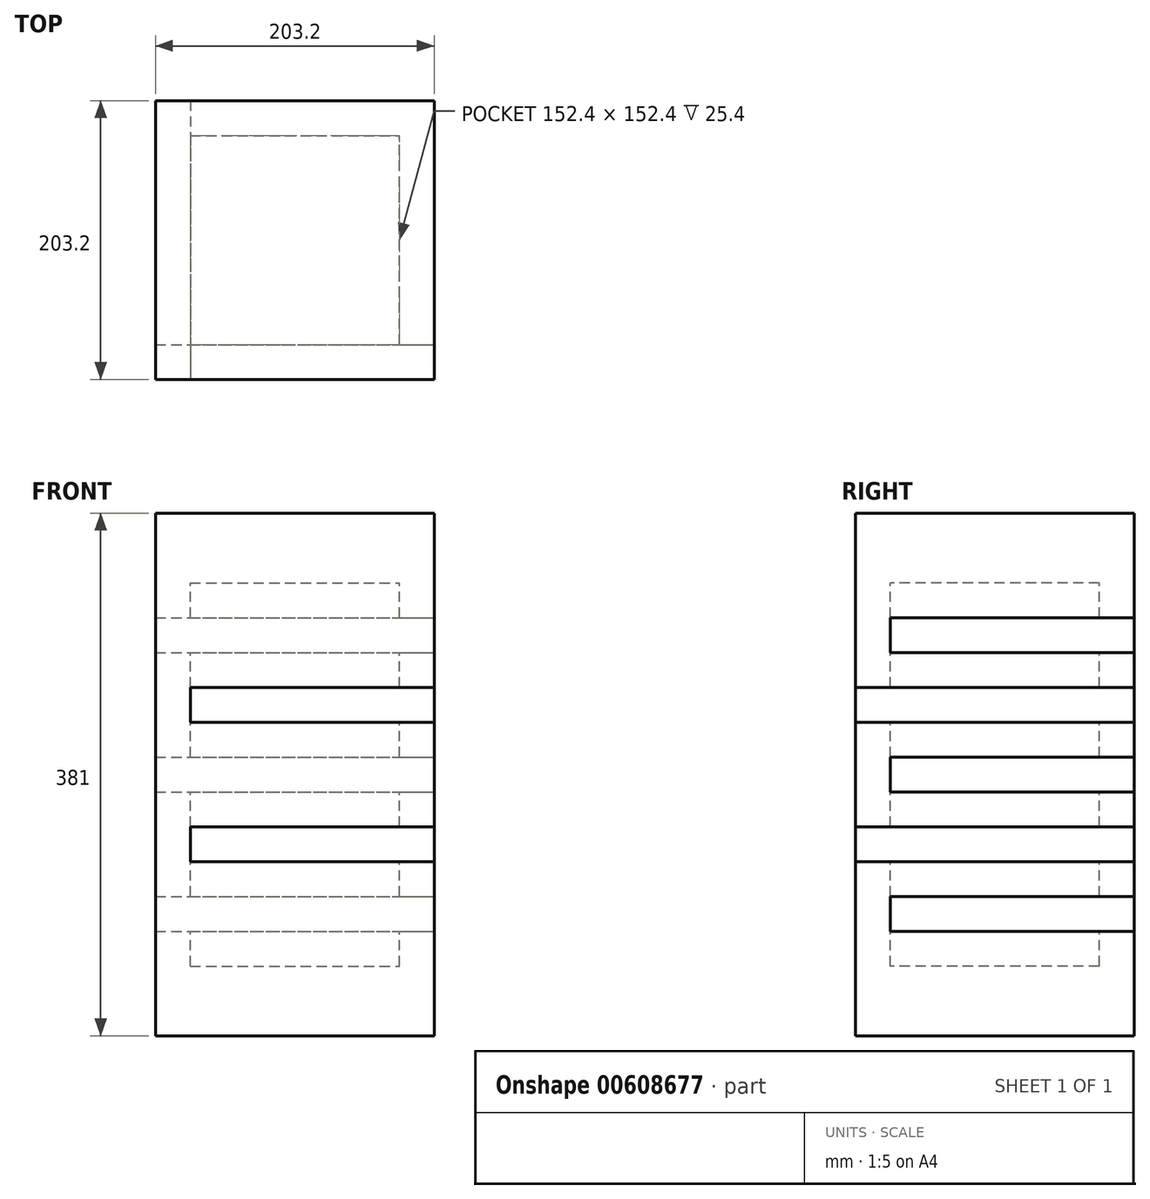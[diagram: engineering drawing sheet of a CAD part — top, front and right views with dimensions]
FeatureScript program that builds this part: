
annotation { "Feature Type Name" : "Feature", "Feature Type Description" : "" }
export const myFeature = defineFeature(function(context is Context, id is Id, definition is map)
    precondition{}
    {
        {
            var Q0;
            Q0=qCreatedBy(makeId("Front.planeOp"),FACE);
            var sketch = newSketch(context, id + "F0", { "sketchPlane" : qUnion([Q0])});
            skLineSegment(sketch, "E0.bottom", {"start": v(0, 0) * mm, "end": v(203.2, 0) * mm});
            skLineSegment(sketch, "E0.top", {"start": v(0, 381) * mm, "end": v(203.2, 381) * mm});
            skLineSegment(sketch, "E0.left", {"start": v(0, 0) * mm, "end": v(0, 381) * mm});
            skLineSegment(sketch, "E0.right", {"start": v(203.2, 0) * mm, "end": v(203.2, 381) * mm});
            skSolve(sketch);
        }
        {
            var Q0;
            Q0=makeQuery(id+"F0.imprint","IMPRINT",FACE,{"disambiguationData":[TD([[makeQuery(id+"F0.imprint","IMPRINT",EDGE,{"derivedFrom":sQuery(id+"F0.wireOp",EDGE,"E0.bottom")}),1.0]])]});
            extrude(context, id + "F1", {"entities" : qUnion([Q0]), "depth" : 203.2 * mm, "offsetDistance" : 25.4 * mm});
        }
        {
            var Q0;
            Q0=makeQuery(id+"F1.opExtrude","CAP_FACE",FACE,{"disambiguationData":[OSD([sQuery(id+"F0.wireOp",EDGE,"E0.bottom"),sQuery(id+"F0.wireOp",EDGE,"E0.top"),sQuery(id+"F0.wireOp",EDGE,"E0.left"),sQuery(id+"F0.wireOp",EDGE,"E0.right")])],"isStart":false});
            var sketch = newSketch(context, id + "F2", { "sketchPlane" : qUnion([Q0])});
            skLineSegment(sketch, "E1.bottom", {"start": v(203.2, 355.6) * mm, "end": v(25.4, 355.6) * mm});
            skLineSegment(sketch, "E1.top", {"start": v(203.2, 330.2) * mm, "end": v(25.4, 330.2) * mm});
            skLineSegment(sketch, "E1.left", {"start": v(203.2, 355.6) * mm, "end": v(203.2, 330.2) * mm});
            skLineSegment(sketch, "E1.right", {"start": v(25.4, 355.6) * mm, "end": v(25.4, 330.2) * mm});
            skLineSegment(sketch, "E2.bottom", {"start": v(203.2, 254) * mm, "end": v(25.4, 254) * mm});
            skLineSegment(sketch, "E2.top", {"start": v(203.2, 228.6) * mm, "end": v(25.4, 228.6) * mm});
            skLineSegment(sketch, "E2.left", {"start": v(203.2, 254) * mm, "end": v(203.2, 228.6) * mm});
            skLineSegment(sketch, "E2.right", {"start": v(25.4, 254) * mm, "end": v(25.4, 228.6) * mm});
            skLineSegment(sketch, "E3.bottom", {"start": v(203.2, 152.4) * mm, "end": v(25.4, 152.4) * mm});
            skLineSegment(sketch, "E3.top", {"start": v(203.2, 127) * mm, "end": v(25.4, 127) * mm});
            skLineSegment(sketch, "E3.left", {"start": v(203.2, 152.4) * mm, "end": v(203.2, 127) * mm});
            skLineSegment(sketch, "E3.right", {"start": v(25.4, 152.4) * mm, "end": v(25.4, 127) * mm});
            skLineSegment(sketch, "E4.bottom", {"start": v(203.2, 50.8) * mm, "end": v(25.4, 50.8) * mm});
            skLineSegment(sketch, "E4.top", {"start": v(203.2, 25.4) * mm, "end": v(25.4, 25.4) * mm});
            skLineSegment(sketch, "E4.left", {"start": v(203.2, 50.8) * mm, "end": v(203.2, 25.4) * mm});
            skLineSegment(sketch, "E4.right", {"start": v(25.4, 50.8) * mm, "end": v(25.4, 25.4) * mm});
            skSolve(sketch);
        }
        {
            var Q0;
            Q0=makeQuery(id+"F2.imprint","IMPRINT",FACE,{"disambiguationData":[TD([[makeQuery(id+"F2.imprint","IMPRINT",EDGE,{"derivedFrom":sQuery(id+"F2.wireOp",EDGE,"E1.bottom")}),1.0]])]});
            var Q1;
            Q1=makeQuery(id+"F2.imprint","IMPRINT",FACE,{"disambiguationData":[TD([[makeQuery(id+"F2.imprint","IMPRINT",EDGE,{"derivedFrom":sQuery(id+"F2.wireOp",EDGE,"E2.bottom")}),1.0]])]});
            var Q2;
            Q2=makeQuery(id+"F2.imprint","IMPRINT",FACE,{"disambiguationData":[TD([[makeQuery(id+"F2.imprint","IMPRINT",EDGE,{"derivedFrom":sQuery(id+"F2.wireOp",EDGE,"E3.bottom")}),1.0]])]});
            var Q3;
            Q3=makeQuery(id+"F2.imprint","IMPRINT",FACE,{"disambiguationData":[TD([[makeQuery(id+"F2.imprint","IMPRINT",EDGE,{"derivedFrom":sQuery(id+"F2.wireOp",EDGE,"E4.bottom")}),1.0]])]});
            extrude(context, id + "F3", {"entities" : qUnion([Q0, Q1, Q2, Q3]), "operationType" : NewBodyOperationType.REMOVE, "endBound" : BoundingType.THROUGH_ALL, "oppositeDirection" : true, "depth" : 25.4 * mm, "offsetDistance" : 25.4 * mm});
        }
        {
            var Q0;
            {var subQ0=sQuery(id+"F0.wireOp",EDGE,"E0.right");Q0=makeQuery(id+"F3.boolean.opBoolean","SPLIT",FACE,{"disambiguationData":[TD([makeQuery(id+"F3.opExtrude","SWEPT_FACE",FACE,{"disambiguationData":[OSD([sQuery(id+"F2.wireOp",EDGE,"E1.top")])]})])],"derivedFrom":makeQuery(id+"F1.opExtrude","SWEPT_FACE",FACE,{"disambiguationData":[OSD([subQ0])]})});}
            var sketch = newSketch(context, id + "F4", { "sketchPlane" : qUnion([Q0])});
            skLineSegment(sketch, "E5.bottom", {"start": v(0, 304.8) * mm, "end": v(-177.8, 304.8) * mm});
            skLineSegment(sketch, "E5.top", {"start": v(0, 279.4) * mm, "end": v(-177.8, 279.4) * mm});
            skLineSegment(sketch, "E5.left", {"start": v(0, 304.8) * mm, "end": v(0, 279.4) * mm});
            skLineSegment(sketch, "E5.right", {"start": v(-177.8, 304.8) * mm, "end": v(-177.8, 279.4) * mm});
            skLineSegment(sketch, "E6.bottom", {"start": v(0, 203.2) * mm, "end": v(-177.8, 203.2) * mm});
            skLineSegment(sketch, "E6.top", {"start": v(0, 177.8) * mm, "end": v(-177.8, 177.8) * mm});
            skLineSegment(sketch, "E6.left", {"start": v(0, 203.2) * mm, "end": v(0, 177.8) * mm});
            skLineSegment(sketch, "E6.right", {"start": v(-177.8, 203.2) * mm, "end": v(-177.8, 177.8) * mm});
            skLineSegment(sketch, "E7.bottom", {"start": v(0, 101.6) * mm, "end": v(-177.8, 101.6) * mm});
            skLineSegment(sketch, "E7.top", {"start": v(0, 76.2) * mm, "end": v(-177.8, 76.2) * mm});
            skLineSegment(sketch, "E7.left", {"start": v(0, 101.6) * mm, "end": v(0, 76.2) * mm});
            skLineSegment(sketch, "E7.right", {"start": v(-177.8, 101.6) * mm, "end": v(-177.8, 76.2) * mm});
            skSolve(sketch);
        }
        {
            var Q0;
            Q0=makeQuery(id+"F4.imprint","IMPRINT",FACE,{"disambiguationData":[TD([[makeQuery(id+"F4.imprint","IMPRINT",EDGE,{"derivedFrom":sQuery(id+"F4.wireOp",EDGE,"E5.bottom")}),1.0]])]});
            var Q1;
            Q1=makeQuery(id+"F4.imprint","IMPRINT",FACE,{"disambiguationData":[TD([[makeQuery(id+"F4.imprint","IMPRINT",EDGE,{"derivedFrom":sQuery(id+"F4.wireOp",EDGE,"E6.bottom")}),1.0]])]});
            var Q2;
            Q2=makeQuery(id+"F4.imprint","IMPRINT",FACE,{"disambiguationData":[TD([[makeQuery(id+"F4.imprint","IMPRINT",EDGE,{"derivedFrom":sQuery(id+"F4.wireOp",EDGE,"E7.bottom")}),1.0]])]});
            extrude(context, id + "F5", {"entities" : qUnion([Q0, Q1, Q2]), "operationType" : NewBodyOperationType.REMOVE, "endBound" : BoundingType.THROUGH_ALL, "oppositeDirection" : true, "depth" : 25.4 * mm, "offsetDistance" : 25.4 * mm});
        }
        {
            var Q0;
            Q0=makeQuery(id+"F1.opExtrude","SWEPT_FACE",FACE,{"disambiguationData":[OSD([sQuery(id+"F0.wireOp",EDGE,"E0.top")])]});
            var sketch = newSketch(context, id + "F6", { "sketchPlane" : qUnion([Q0])});
            skLineSegment(sketch, "E8.0", {"start": v(25.4, -177.8) * mm, "end": v(25.4, -25.4) * mm});
            skLineSegment(sketch, "E8.1", {"start": v(25.4, -177.8) * mm, "end": v(177.8, -177.8) * mm});
            skLineSegment(sketch, "E8.2", {"start": v(177.8, -177.8) * mm, "end": v(177.8, -25.4) * mm});
            skLineSegment(sketch, "E8.3", {"start": v(25.4, -25.4) * mm, "end": v(177.8, -25.4) * mm});
            skSolve(sketch);
        }
        {
            var Q0;
            Q0=makeQuery(id+"F6.imprint","IMPRINT",FACE,{"disambiguationData":[TD([[makeQuery(id+"F6.imprint","IMPRINT",EDGE,{"derivedFrom":sQuery(id+"F6.wireOp",EDGE,"E8.0")}),-1.0]])]});
            extrude(context, id + "F7", {"entities" : qUnion([Q0]), "operationType" : NewBodyOperationType.REMOVE, "endBound" : BoundingType.THROUGH_ALL, "oppositeDirection" : true, "depth" : 25.4 * mm, "offsetDistance" : 25.4 * mm});
        }
        {
            var Q0;
            Q0=makeQuery(id+"F2.imprint","IMPRINT",FACE,{"disambiguationData":[TD([[makeQuery(id+"F2.imprint","IMPRINT",EDGE,{"derivedFrom":sQuery(id+"F2.wireOp",EDGE,"E1.bottom")}),1.0]])]});
            var Q1;
            Q1=makeQuery(id+"F2.imprint","IMPRINT",FACE,{"disambiguationData":[TD([[makeQuery(id+"F2.imprint","IMPRINT",EDGE,{"derivedFrom":sQuery(id+"F2.wireOp",EDGE,"E2.bottom")}),1.0]])]});
            var Q2;
            Q2=makeQuery(id+"F2.imprint","IMPRINT",FACE,{"disambiguationData":[TD([[makeQuery(id+"F2.imprint","IMPRINT",EDGE,{"derivedFrom":sQuery(id+"F2.wireOp",EDGE,"E3.bottom")}),1.0]])]});
            var Q3;
            Q3=makeQuery(id+"F2.imprint","IMPRINT",FACE,{"disambiguationData":[TD([[makeQuery(id+"F2.imprint","IMPRINT",EDGE,{"derivedFrom":sQuery(id+"F2.wireOp",EDGE,"E4.bottom")}),1.0]])]});
            extrude(context, id + "F8", {"entities" : qUnion([Q0, Q1, Q2, Q3]), "oppositeDirection" : true, "depth" : 203.2 * mm, "offsetDistance" : 25.4 * mm});
        }
        {
            var Q0;
            Q0=makeQuery(id+"F4.imprint","IMPRINT",FACE,{"disambiguationData":[TD([[makeQuery(id+"F4.imprint","IMPRINT",EDGE,{"derivedFrom":sQuery(id+"F4.wireOp",EDGE,"E5.bottom")}),1.0]])]});
            var Q1;
            Q1=makeQuery(id+"F4.imprint","IMPRINT",FACE,{"disambiguationData":[TD([[makeQuery(id+"F4.imprint","IMPRINT",EDGE,{"derivedFrom":sQuery(id+"F4.wireOp",EDGE,"E6.bottom")}),1.0]])]});
            var Q2;
            Q2=makeQuery(id+"F4.imprint","IMPRINT",FACE,{"disambiguationData":[TD([[makeQuery(id+"F4.imprint","IMPRINT",EDGE,{"derivedFrom":sQuery(id+"F4.wireOp",EDGE,"E7.bottom")}),1.0]])]});
            extrude(context, id + "F9", {"entities" : qUnion([Q0, Q1, Q2]), "oppositeDirection" : true, "depth" : 203.2 * mm, "offsetDistance" : 25.4 * mm});
        }
        {
            var Q0;
            Q0=makeQuery(id+"F7.boolean.opBoolean","COPY",FACE,{"disambiguationData":[TD([makeQuery(id+"F1.opExtrude","SWEPT_FACE",FACE,{"disambiguationData":[OSD([sQuery(id+"F0.wireOp",EDGE,"E0.top")])]})])],"derivedFrom":makeQuery(id+"F7.opExtrude","SWEPT_FACE",FACE,{"disambiguationData":[OSD([sQuery(id+"F6.wireOp",EDGE,"E8.1")])]})});
            extrude(context, id + "F10", {"entities" : qUnion([Q0]), "operationType" : NewBodyOperationType.ADD, "endBound" : BoundingType.UP_TO_NEXT, "depth" : 25.4 * mm, "offsetDistance" : 25.4 * mm});
        }
        {
            var Q0;
            Q0=makeQuery(id+"F7.boolean.opBoolean","COPY",FACE,{"disambiguationData":[TD([makeQuery(id+"F1.opExtrude","SWEPT_FACE",FACE,{"disambiguationData":[OSD([sQuery(id+"F0.wireOp",EDGE,"E0.bottom")])]})])],"derivedFrom":makeQuery(id+"F7.opExtrude","SWEPT_FACE",FACE,{"disambiguationData":[OSD([sQuery(id+"F6.wireOp",EDGE,"E8.1")])]})});
            extrude(context, id + "F11", {"entities" : qUnion([Q0]), "operationType" : NewBodyOperationType.ADD, "endBound" : BoundingType.UP_TO_NEXT, "depth" : 25.4 * mm, "offsetDistance" : 25.4 * mm});
        }
    });
